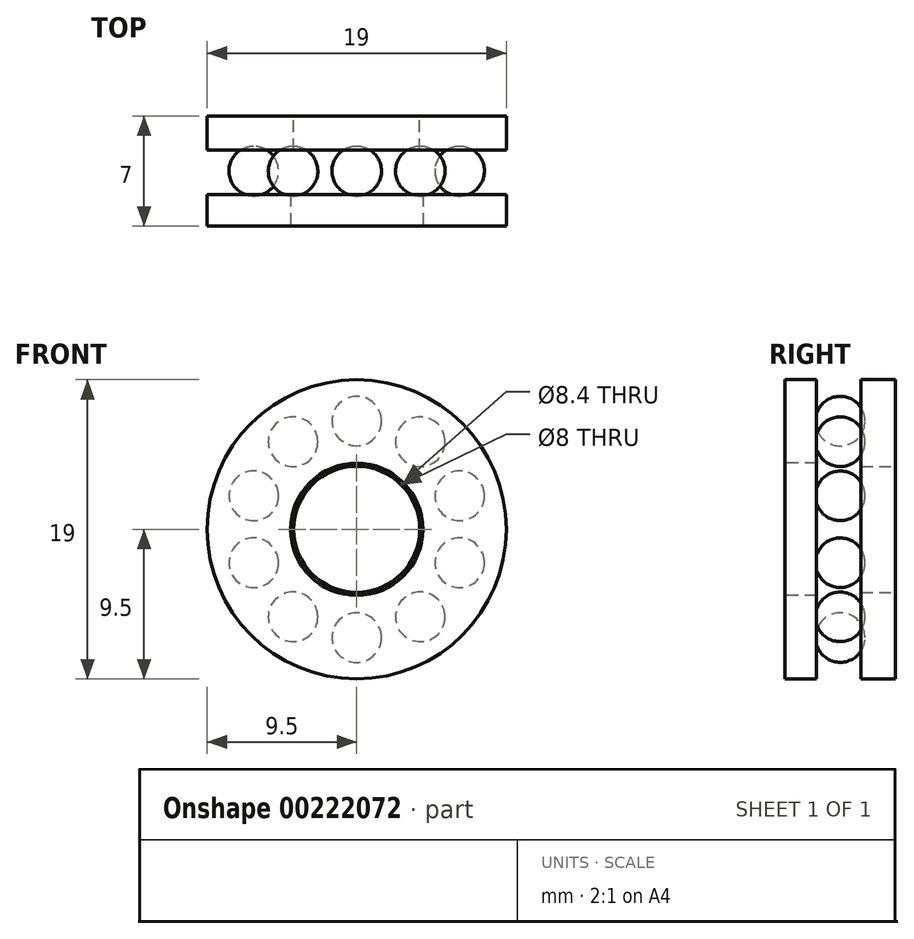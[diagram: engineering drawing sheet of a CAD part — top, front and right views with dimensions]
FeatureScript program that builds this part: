
annotation { "Feature Type Name" : "Feature", "Feature Type Description" : "" }
export const myFeature = defineFeature(function(context is Context, id is Id, definition is map)
    precondition{}
    {
        {
            var Q0;
            Q0=qCreatedBy(makeId("Front.planeOp"),FACE);
            var sketch = newSketch(context, id + "F0", { "sketchPlane" : qUnion([Q0])});
            skCircle(sketch, "E0", {"center": v(0, 0) * mm, "radius": 9.5 * mm});
            skCircle(sketch, "E1", {"center": v(0, 0) * mm, "radius": 4 * mm});
            skSolve(sketch);
        }
        {
            var Q0;
            Q0=makeQuery(id+"F0.imprint","IMPRINT",FACE,{"disambiguationData":[TD([[makeQuery(id+"F0.imprint","IMPRINT",EDGE,{"derivedFrom":sQuery(id+"F0.wireOp",EDGE,"E0")}),1.0]])]});
            extrude(context, id + "F1", {"entities" : qUnion([Q0]), "depth" : 2.17 * mm});
        }
        {
            var Q0;
            Q0=qCreatedBy(makeId("Front.planeOp"),FACE);
            cPlane(context, id + "F2", {"entities" : qUnion([Q0]), "cplaneType" : CPlaneType.OFFSET, "offset" : 7 * mm, "width" : 150 * mm, "height" : 150 * mm});
        }
        {
            var Q0;
            Q0=qCreatedBy(id+"F2.planeOp",FACE);
            var sketch = newSketch(context, id + "F3", { "sketchPlane" : qUnion([Q0])});
            skCircle(sketch, "E2.0", {"center": v(0, 0) * mm, "radius": 9.5 * mm});
            skCircle(sketch, "E3", {"center": v(0, 0) * mm, "radius": 4.2 * mm});
            skSolve(sketch);
        }
        {
            var Q0;
            Q0=makeQuery(id+"F3.imprint","IMPRINT",FACE,{"disambiguationData":[TD([[makeQuery(id+"F3.imprint","IMPRINT",EDGE,{"derivedFrom":sQuery(id+"F3.wireOp",EDGE,"E2.0")}),1.0]])]});
            extrude(context, id + "F4", {"entities" : qUnion([Q0]), "oppositeDirection" : true, "depth" : 2 * mm});
        }
        {
            var Q0;
            Q0=qCreatedBy(makeId("Front.planeOp"),FACE);
            cPlane(context, id + "F5", {"entities" : qUnion([Q0]), "cplaneType" : CPlaneType.OFFSET, "offset" : 3.5 * mm, "width" : 150 * mm, "height" : 150 * mm});
        }
        {
            var Q0;
            Q0=qCreatedBy(id+"F5.planeOp",FACE);
            var sketch = newSketch(context, id + "F6", { "sketchPlane" : qUnion([Q0])});
            skCircle(sketch, "E4", {"center": v(0, 0) * mm, "radius": 6.88 * mm, "construction": true});
            skCircle(sketch, "E5", {"center": v(0, 6.88) * mm, "radius": 1.57 * mm});
            skCircle(sketch, "E6.1.0", {"center": v(-4.04, 5.56) * mm, "radius": 1.57 * mm});
            skCircle(sketch, "E6.2.0", {"center": v(-6.54, 2.12) * mm, "radius": 1.57 * mm});
            skCircle(sketch, "E6.3.0", {"center": v(-6.54, -2.12) * mm, "radius": 1.57 * mm});
            skCircle(sketch, "E6.4.0", {"center": v(-4.04, -5.56) * mm, "radius": 1.57 * mm});
            skCircle(sketch, "E6.5.0", {"center": v(0, -6.88) * mm, "radius": 1.57 * mm});
            skCircle(sketch, "E6.6.0", {"center": v(4.04, -5.56) * mm, "radius": 1.57 * mm});
            skCircle(sketch, "E6.7.0", {"center": v(6.54, -2.12) * mm, "radius": 1.57 * mm});
            skCircle(sketch, "E6.8.0", {"center": v(6.54, 2.12) * mm, "radius": 1.57 * mm});
            skCircle(sketch, "E6.9.0", {"center": v(4.04, 5.56) * mm, "radius": 1.57 * mm});
            skSolve(sketch);
        }
        {
            var Q0;
            Q0=makeQuery(id+"F6.imprint","IMPRINT",FACE,{"disambiguationData":[TD([[makeQuery(id+"F6.imprint","IMPRINT",EDGE,{"derivedFrom":sQuery(id+"F6.wireOp",EDGE,"E6.3.0")}),1.0]])]});
            var Q1;
            Q1=makeQuery(id+"F6.imprint","IMPRINT",FACE,{"disambiguationData":[TD([[makeQuery(id+"F6.imprint","IMPRINT",EDGE,{"derivedFrom":sQuery(id+"F6.wireOp",EDGE,"E6.4.0")}),1.0]])]});
            var Q2;
            Q2=makeQuery(id+"F6.imprint","IMPRINT",FACE,{"disambiguationData":[TD([[makeQuery(id+"F6.imprint","IMPRINT",EDGE,{"derivedFrom":sQuery(id+"F6.wireOp",EDGE,"E6.5.0")}),1.0]])]});
            var Q3;
            Q3=makeQuery(id+"F6.imprint","IMPRINT",FACE,{"disambiguationData":[TD([[makeQuery(id+"F6.imprint","IMPRINT",EDGE,{"derivedFrom":sQuery(id+"F6.wireOp",EDGE,"E6.6.0")}),1.0]])]});
            var Q4;
            Q4=makeQuery(id+"F6.imprint","IMPRINT",FACE,{"disambiguationData":[TD([[makeQuery(id+"F6.imprint","IMPRINT",EDGE,{"derivedFrom":sQuery(id+"F6.wireOp",EDGE,"E6.7.0")}),1.0]])]});
            var Q5;
            Q5=makeQuery(id+"F6.imprint","IMPRINT",FACE,{"disambiguationData":[TD([[makeQuery(id+"F6.imprint","IMPRINT",EDGE,{"derivedFrom":sQuery(id+"F6.wireOp",EDGE,"E6.8.0")}),1.0]])]});
            var Q6;
            Q6=makeQuery(id+"F6.imprint","IMPRINT",FACE,{"disambiguationData":[TD([[makeQuery(id+"F6.imprint","IMPRINT",EDGE,{"derivedFrom":sQuery(id+"F6.wireOp",EDGE,"E6.9.0")}),1.0]])]});
            var Q7;
            Q7=makeQuery(id+"F6.imprint","IMPRINT",FACE,{"disambiguationData":[TD([[makeQuery(id+"F6.imprint","IMPRINT",EDGE,{"derivedFrom":sQuery(id+"F6.wireOp",EDGE,"E5")}),1.0]])]});
            var Q8;
            Q8=makeQuery(id+"F6.imprint","IMPRINT",FACE,{"disambiguationData":[TD([[makeQuery(id+"F6.imprint","IMPRINT",EDGE,{"derivedFrom":sQuery(id+"F6.wireOp",EDGE,"E6.1.0")}),1.0]])]});
            var Q9;
            Q9=makeQuery(id+"F6.imprint","IMPRINT",FACE,{"disambiguationData":[TD([[makeQuery(id+"F6.imprint","IMPRINT",EDGE,{"derivedFrom":sQuery(id+"F6.wireOp",EDGE,"E6.2.0")}),1.0]])]});
            extrude(context, id + "F7", {"entities" : qUnion([Q0, Q1, Q2, Q3, Q4, Q5, Q6, Q7, Q8, Q9]), "depth" : (3.15 / 2) * mm, "hasSecondDirection" : true, "secondDirectionOppositeDirection" : true, "secondDirectionDepth" : (3.15 / 2) * mm});
        }
        {
            var Q0;
            Q0=makeQuery(id+"F7.opExtrude","CAP_EDGE",EDGE,{"disambiguationData":[OSD([sQuery(id+"F6.wireOp",EDGE,"E5")])],"isStart":true});
            var Q1;
            Q1=makeQuery(id+"F7.opExtrude","CAP_EDGE",EDGE,{"disambiguationData":[OSD([sQuery(id+"F6.wireOp",EDGE,"E5")])],"isStart":false});
            var Q2;
            Q2=makeQuery(id+"F7.opExtrude","CAP_EDGE",EDGE,{"disambiguationData":[OSD([sQuery(id+"F6.wireOp",EDGE,"E6.9.0")])],"isStart":true});
            var Q3;
            Q3=makeQuery(id+"F7.opExtrude","CAP_EDGE",EDGE,{"disambiguationData":[OSD([sQuery(id+"F6.wireOp",EDGE,"E6.9.0")])],"isStart":false});
            var Q4;
            Q4=makeQuery(id+"F7.opExtrude","CAP_EDGE",EDGE,{"disambiguationData":[OSD([sQuery(id+"F6.wireOp",EDGE,"E6.8.0")])],"isStart":true});
            var Q5;
            Q5=makeQuery(id+"F7.opExtrude","CAP_EDGE",EDGE,{"disambiguationData":[OSD([sQuery(id+"F6.wireOp",EDGE,"E6.8.0")])],"isStart":false});
            var Q6;
            Q6=makeQuery(id+"F7.opExtrude","CAP_EDGE",EDGE,{"disambiguationData":[OSD([sQuery(id+"F6.wireOp",EDGE,"E6.1.0")])],"isStart":true});
            var Q7;
            Q7=makeQuery(id+"F7.opExtrude","CAP_EDGE",EDGE,{"disambiguationData":[OSD([sQuery(id+"F6.wireOp",EDGE,"E6.1.0")])],"isStart":false});
            var Q8;
            Q8=makeQuery(id+"F7.opExtrude","CAP_EDGE",EDGE,{"disambiguationData":[OSD([sQuery(id+"F6.wireOp",EDGE,"E6.2.0")])],"isStart":true});
            var Q9;
            Q9=makeQuery(id+"F7.opExtrude","CAP_EDGE",EDGE,{"disambiguationData":[OSD([sQuery(id+"F6.wireOp",EDGE,"E6.2.0")])],"isStart":false});
            var Q10;
            Q10=makeQuery(id+"F7.opExtrude","CAP_EDGE",EDGE,{"disambiguationData":[OSD([sQuery(id+"F6.wireOp",EDGE,"E6.3.0")])],"isStart":true});
            var Q11;
            Q11=makeQuery(id+"F7.opExtrude","CAP_EDGE",EDGE,{"disambiguationData":[OSD([sQuery(id+"F6.wireOp",EDGE,"E6.3.0")])],"isStart":false});
            var Q12;
            Q12=makeQuery(id+"F7.opExtrude","CAP_EDGE",EDGE,{"disambiguationData":[OSD([sQuery(id+"F6.wireOp",EDGE,"E6.4.0")])],"isStart":true});
            var Q13;
            Q13=makeQuery(id+"F7.opExtrude","CAP_EDGE",EDGE,{"disambiguationData":[OSD([sQuery(id+"F6.wireOp",EDGE,"E6.4.0")])],"isStart":false});
            var Q14;
            Q14=makeQuery(id+"F7.opExtrude","CAP_EDGE",EDGE,{"disambiguationData":[OSD([sQuery(id+"F6.wireOp",EDGE,"E6.5.0")])],"isStart":true});
            var Q15;
            Q15=makeQuery(id+"F7.opExtrude","CAP_EDGE",EDGE,{"disambiguationData":[OSD([sQuery(id+"F6.wireOp",EDGE,"E6.5.0")])],"isStart":false});
            var Q16;
            Q16=makeQuery(id+"F7.opExtrude","CAP_EDGE",EDGE,{"disambiguationData":[OSD([sQuery(id+"F6.wireOp",EDGE,"E6.6.0")])],"isStart":true});
            var Q17;
            Q17=makeQuery(id+"F7.opExtrude","CAP_EDGE",EDGE,{"disambiguationData":[OSD([sQuery(id+"F6.wireOp",EDGE,"E6.7.0")])],"isStart":true});
            var Q18;
            Q18=makeQuery(id+"F7.opExtrude","SWEPT_FACE",FACE,{"disambiguationData":[OSD([sQuery(id+"F6.wireOp",EDGE,"E6.4.0")])]});
            var Q19;
            Q19=makeQuery(id+"F7.opExtrude","CAP_EDGE",EDGE,{"disambiguationData":[OSD([sQuery(id+"F6.wireOp",EDGE,"E6.7.0")])],"isStart":false});
            var Q20;
            Q20=makeQuery(id+"F7.opExtrude","CAP_EDGE",EDGE,{"disambiguationData":[OSD([sQuery(id+"F6.wireOp",EDGE,"E6.6.0")])],"isStart":false});
            fillet(context, id + "F8", {"entities" : qUnion([Q0, Q1, Q2, Q3, Q4, Q5, Q6, Q7, Q8, Q9, Q10, Q11, Q12, Q13, Q14, Q15, Q16, Q17, Q18, Q19, Q20]), "radius" : 3.15 / 2 * mm, "tangentPropagation" : true, "allowEdgeOverflow" : false});
        }
    });
